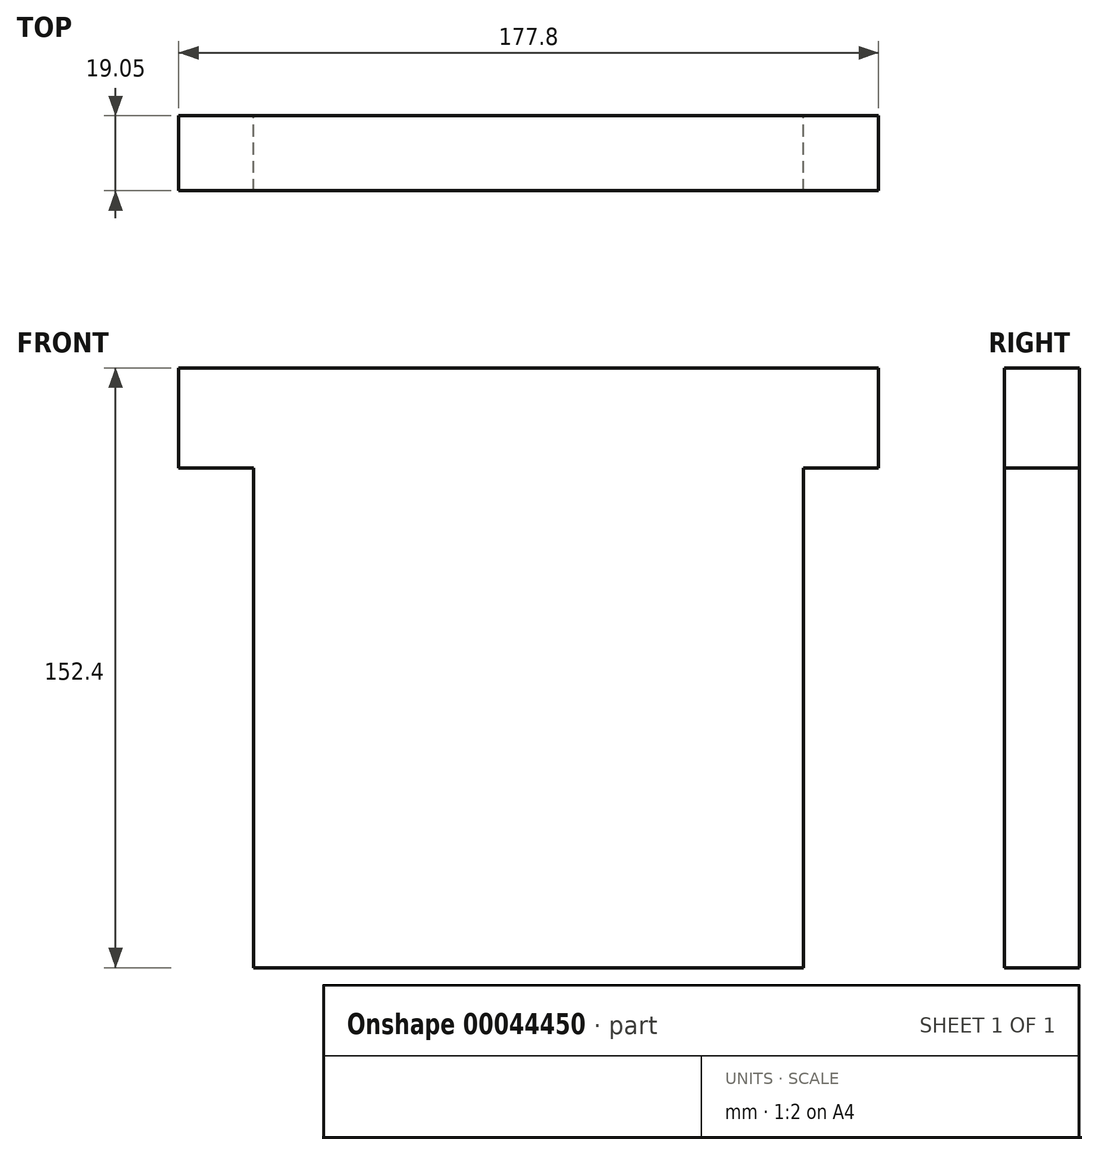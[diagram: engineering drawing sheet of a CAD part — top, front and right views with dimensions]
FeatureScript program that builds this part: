
annotation { "Feature Type Name" : "Feature", "Feature Type Description" : "" }
export const myFeature = defineFeature(function(context is Context, id is Id, definition is map)
    precondition{}
    {
        {
            var Q0;
            Q0=qCreatedBy(makeId("Front.planeOp"),FACE);
            var sketch = newSketch(context, id + "F0", { "sketchPlane" : qUnion([Q0])});
            skLineSegment(sketch, "E0.bottom", {"start": v(-92.53, 71.48) * mm, "end": v(47.17, 71.48) * mm});
            skLineSegment(sketch, "E0.top", {"start": v(-92.53, -80.92) * mm, "end": v(47.17, -80.92) * mm});
            skLineSegment(sketch, "E0.left", {"start": v(-92.53, 71.48) * mm, "end": v(-92.53, -80.92) * mm});
            skLineSegment(sketch, "E0.right", {"start": v(47.17, 71.48) * mm, "end": v(47.17, -80.92) * mm});
            skLineSegment(sketch, "E1.bottom", {"start": v(-92.53, 71.48) * mm, "end": v(-111.58, 71.48) * mm});
            skLineSegment(sketch, "E1.top", {"start": v(-92.53, 46.08) * mm, "end": v(-111.58, 46.08) * mm});
            skLineSegment(sketch, "E1.left", {"start": v(-92.53, 71.48) * mm, "end": v(-92.53, 46.08) * mm});
            skLineSegment(sketch, "E1.right", {"start": v(-111.58, 71.48) * mm, "end": v(-111.58, 46.08) * mm});
            skLineSegment(sketch, "E2.bottom", {"start": v(47.17, 71.48) * mm, "end": v(66.22, 71.48) * mm});
            skLineSegment(sketch, "E2.top", {"start": v(47.17, 46.08) * mm, "end": v(66.22, 46.08) * mm});
            skLineSegment(sketch, "E2.left", {"start": v(47.17, 71.48) * mm, "end": v(47.17, 46.08) * mm});
            skLineSegment(sketch, "E2.right", {"start": v(66.22, 71.48) * mm, "end": v(66.22, 46.08) * mm});
            skSolve(sketch);
        }
        {
            var Q0;
            Q0=makeQuery(id+"F0.imprint","IMPRINT",FACE,{"disambiguationData":[TD([[makeQuery(id+"F0.imprint","IMPRINT",EDGE,{"derivedFrom":sQuery(id+"F0.wireOp",EDGE,"E1.bottom")}),1.0]])]});
            var Q1;
            Q1=makeQuery(id+"F0.imprint","IMPRINT",FACE,{"disambiguationData":[TD([[makeQuery(id+"F0.imprint","IMPRINT",EDGE,{"derivedFrom":sQuery(id+"F0.wireOp",EDGE,"E0.bottom")}),-1.0]])]});
            var Q2;
            Q2=makeQuery(id+"F0.imprint","IMPRINT",FACE,{"disambiguationData":[TD([[makeQuery(id+"F0.imprint","IMPRINT",EDGE,{"derivedFrom":sQuery(id+"F0.wireOp",EDGE,"E2.bottom")}),-1.0]])]});
            extrude(context, id + "F1", {"entities" : qUnion([Q0, Q1, Q2]), "depth" : 19.05 * mm});
        }
    });
